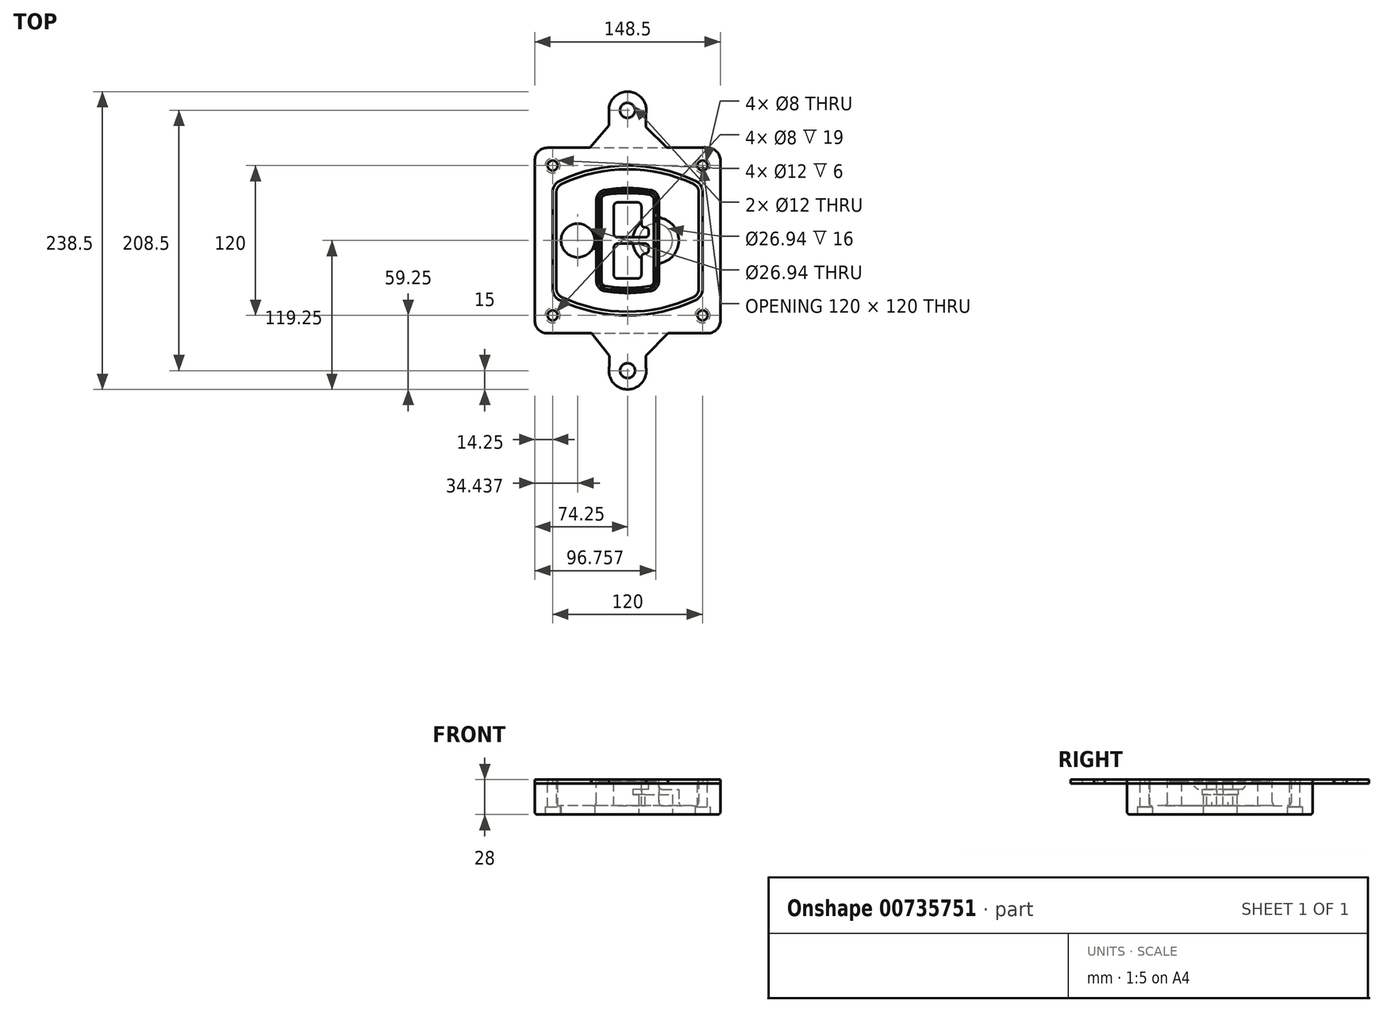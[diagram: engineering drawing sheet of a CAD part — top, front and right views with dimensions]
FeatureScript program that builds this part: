
annotation { "Feature Type Name" : "Feature", "Feature Type Description" : "" }
export const myFeature = defineFeature(function(context is Context, id is Id, definition is map)
    precondition{}
    {
        {
            var Q0;
            Q0=qCreatedBy(makeId("Top.planeOp"),FACE);
            var sketch = newSketch(context, id + "F0", { "sketchPlane" : qUnion([Q0])});
            skPoint(sketch, "E0.rect.middle", {"position": v(0, 0) * mm});
            skLineSegment(sketch, "E1.bottom", {"start": v(-64.25, -74.25) * mm, "end": v(64.25, -74.25) * mm});
            skLineSegment(sketch, "E1.top", {"start": v(-64.25, 74.25) * mm, "end": v(64.25, 74.25) * mm});
            skLineSegment(sketch, "E1.left", {"start": v(-74.25, -64.25) * mm, "end": v(-74.25, 64.25) * mm});
            skLineSegment(sketch, "E1.right", {"start": v(74.25, -64.25) * mm, "end": v(74.25, 64.25) * mm});
            skLineSegment(sketch, "E2", {"start": v(-74.25, 74.25) * mm, "end": v(74.25, -74.25) * mm, "construction": true});
            skLineSegment(sketch, "E3", {"start": v(74.25, 74.25) * mm, "end": v(-74.25, -74.25) * mm, "construction": true});
            skCircle(sketch, "E4", {"center": v(-60, 60) * mm, "radius": 4 * mm});
            skCircle(sketch, "E5", {"center": v(60, 60) * mm, "radius": 4 * mm});
            skCircle(sketch, "E6", {"center": v(60, -60) * mm, "radius": 4 * mm});
            skCircle(sketch, "E7", {"center": v(-60, -60) * mm, "radius": 4 * mm});
            skLineSegment(sketch, "E8", {"start": v(-60, 60) * mm, "end": v(60, 60) * mm, "construction": true});
            skLineSegment(sketch, "E9", {"start": v(60, 60) * mm, "end": v(60, -60) * mm, "construction": true});
            skLineSegment(sketch, "E10", {"start": v(60, -60) * mm, "end": v(-60, -60) * mm, "construction": true});
            skLineSegment(sketch, "E11", {"start": v(-60, -60) * mm, "end": v(-60, 60) * mm, "construction": true});
            skLineSegment(sketch, "E12", {"start": v(-60, 38.83) * mm, "end": v(-60, -38.83) * mm});
            skLineSegment(sketch, "E13", {"start": v(60, 38.83) * mm, "end": v(60, -38.83) * mm});
            skArc(sketch, "E14", {"start": v(54.26, 47.88) * mm, "mid": v(0, 60) * mm, "end": v(-54.26, 47.88) * mm});
            skArc(sketch, "E15", {"start": v(-54.26, -47.88) * mm, "mid": v(0, -60) * mm, "end": v(54.26, -47.88) * mm});
            skLineSegment(sketch, "E16", {"start": v(-60, 0) * mm, "end": v(60, 0) * mm, "construction": true});
            skPoint(sketch, "E17.visualSharp", {"position": v(-60, -45) * mm});
            skArc(sketch, "E17.filletArc", {"start": v(-60, -38.83) * mm, "mid": v(-58.44, -44.2) * mm, "end": v(-54.26, -47.88) * mm});
            skPoint(sketch, "E18.visualSharp", {"position": v(-60, 45) * mm});
            skArc(sketch, "E18.filletArc", {"start": v(-54.26, 47.88) * mm, "mid": v(-58.44, 44.2) * mm, "end": v(-60, 38.83) * mm});
            skPoint(sketch, "E19.visualSharp", {"position": v(60, 45) * mm});
            skArc(sketch, "E19.filletArc", {"start": v(60, 38.83) * mm, "mid": v(58.44, 44.2) * mm, "end": v(54.26, 47.88) * mm});
            skPoint(sketch, "E20.visualSharp", {"position": v(60, -45) * mm});
            skArc(sketch, "E20.filletArc", {"start": v(54.26, -47.88) * mm, "mid": v(58.44, -44.2) * mm, "end": v(60, -38.83) * mm});
            skPoint(sketch, "E21.visualSharp", {"position": v(-74.25, 74.25) * mm});
            skArc(sketch, "E21.filletArc", {"start": v(-64.25, 74.25) * mm, "mid": v(-71.32, 71.32) * mm, "end": v(-74.25, 64.25) * mm});
            skPoint(sketch, "E22.visualSharp", {"position": v(74.25, 74.25) * mm});
            skArc(sketch, "E22.filletArc", {"start": v(74.25, 64.25) * mm, "mid": v(71.32, 71.32) * mm, "end": v(64.25, 74.25) * mm});
            skPoint(sketch, "E23.visualSharp", {"position": v(74.25, -74.25) * mm});
            skArc(sketch, "E23.filletArc", {"start": v(64.25, -74.25) * mm, "mid": v(71.32, -71.32) * mm, "end": v(74.25, -64.25) * mm});
            skPoint(sketch, "E24.visualSharp", {"position": v(-74.25, -74.25) * mm});
            skArc(sketch, "E24.filletArc", {"start": v(-74.25, -64.25) * mm, "mid": v(-71.32, -71.32) * mm, "end": v(-64.25, -74.25) * mm});
            skArc(sketch, "E25.0", {"start": v(57, 38.83) * mm, "mid": v(55.9, 42.58) * mm, "end": v(52.98, 45.17) * mm});
            skLineSegment(sketch, "E25.1", {"start": v(57, 38.83) * mm, "end": v(57, -38.83) * mm});
            skArc(sketch, "E25.2", {"start": v(52.98, -45.17) * mm, "mid": v(55.9, -42.58) * mm, "end": v(57, -38.83) * mm});
            skArc(sketch, "E25.3", {"start": v(-52.98, -45.17) * mm, "mid": v(0, -57) * mm, "end": v(52.98, -45.17) * mm});
            skArc(sketch, "E25.4", {"start": v(-57, -38.83) * mm, "mid": v(-55.9, -42.58) * mm, "end": v(-52.98, -45.17) * mm});
            skArc(sketch, "E25.5", {"start": v(52.98, 45.17) * mm, "mid": v(0, 57) * mm, "end": v(-52.98, 45.17) * mm});
            skLineSegment(sketch, "E25.6", {"start": v(-57, 38.83) * mm, "end": v(-57, -38.83) * mm});
            skArc(sketch, "E25.7", {"start": v(-52.98, 45.17) * mm, "mid": v(-55.9, 42.58) * mm, "end": v(-57, 38.83) * mm});
            skArc(sketch, "E26.0", {"start": v(-55.96, 51.5) * mm, "mid": v(-61.82, 46.33) * mm, "end": v(-64, 38.83) * mm});
            skArc(sketch, "E26.1", {"start": v(55.96, 51.5) * mm, "mid": v(0, 64) * mm, "end": v(-55.96, 51.5) * mm});
            skArc(sketch, "E26.2", {"start": v(64, 38.83) * mm, "mid": v(61.82, 46.33) * mm, "end": v(55.96, 51.5) * mm});
            skLineSegment(sketch, "E26.3", {"start": v(64, 38.83) * mm, "end": v(64, -38.83) * mm});
            skArc(sketch, "E26.4", {"start": v(55.96, -51.5) * mm, "mid": v(61.82, -46.33) * mm, "end": v(64, -38.83) * mm});
            skLineSegment(sketch, "E26.5", {"start": v(-64, 38.83) * mm, "end": v(-64, -38.83) * mm});
            skArc(sketch, "E26.6", {"start": v(-55.96, -51.5) * mm, "mid": v(0, -64) * mm, "end": v(55.96, -51.5) * mm});
            skArc(sketch, "E26.7", {"start": v(-64, -38.83) * mm, "mid": v(-61.82, -46.33) * mm, "end": v(-55.96, -51.5) * mm});
            skSolve(sketch);
        }
        {
            var Q0;
            Q0=makeQuery(id+"F0.imprint","IMPRINT",FACE,{"disambiguationData":[TD([[makeQuery(id+"F0.imprint","IMPRINT",EDGE,{"derivedFrom":sQuery(id+"F0.wireOp",EDGE,"E1.bottom")}),1.0]])]});
            var Q1;
            Q1=makeQuery(id+"F0.imprint","IMPRINT",FACE,{"disambiguationData":[TD([[makeQuery(id+"F0.imprint","IMPRINT",EDGE,{"derivedFrom":sQuery(id+"F0.wireOp",EDGE,"E12")}),1.0]])]});
            var Q2;
            Q2=makeQuery(id+"F0.imprint","IMPRINT",FACE,{"disambiguationData":[TD([[makeQuery(id+"F0.imprint","IMPRINT",EDGE,{"derivedFrom":sQuery(id+"F0.wireOp",EDGE,"E25.0")}),1.0]])]});
            var Q3;
            Q3=makeQuery(id+"F0.imprint","IMPRINT",FACE,{"disambiguationData":[TD([[makeQuery(id+"F0.imprint","IMPRINT",EDGE,{"derivedFrom":sQuery(id+"F0.wireOp",EDGE,"E12")}),-1.0]])]});
            extrude(context, id + "F1", {"entities" : qUnion([Q0, Q1, Q2, Q3]), "oppositeDirection" : true, "depth" : 25 * mm});
        }
        {
            var Q0;
            Q0=makeQuery(id+"F0.imprint","IMPRINT",FACE,{"disambiguationData":[TD([[makeQuery(id+"F0.imprint","IMPRINT",EDGE,{"derivedFrom":sQuery(id+"F0.wireOp",EDGE,"E12")}),1.0]])]});
            extrude(context, id + "F2", {"entities" : qUnion([Q0]), "operationType" : NewBodyOperationType.ADD, "depth" : 3 * mm});
        }
        {
            var Q0;
            Q0=makeQuery(id+"F0.imprint","IMPRINT",FACE,{"disambiguationData":[TD([[makeQuery(id+"F0.imprint","IMPRINT",EDGE,{"derivedFrom":sQuery(id+"F0.wireOp",EDGE,"E25.0")}),1.0]])]});
            extrude(context, id + "F3", {"entities" : qUnion([Q0]), "operationType" : NewBodyOperationType.REMOVE, "oppositeDirection" : true, "depth" : 18 * mm});
        }
        {
            var Q0;
            Q0=makeQuery(id+"F2.opExtrude","CAP_FACE",FACE,{"disambiguationData":[OSD([sQuery(id+"F0.wireOp",EDGE,"E12"),sQuery(id+"F0.wireOp",EDGE,"E13"),sQuery(id+"F0.wireOp",EDGE,"E14"),sQuery(id+"F0.wireOp",EDGE,"E15"),sQuery(id+"F0.wireOp",EDGE,"E17.filletArc"),sQuery(id+"F0.wireOp",EDGE,"E18.filletArc"),sQuery(id+"F0.wireOp",EDGE,"E19.filletArc"),sQuery(id+"F0.wireOp",EDGE,"E20.filletArc"),sQuery(id+"F0.wireOp",EDGE,"E25.0"),sQuery(id+"F0.wireOp",EDGE,"E25.1"),sQuery(id+"F0.wireOp",EDGE,"E25.2"),sQuery(id+"F0.wireOp",EDGE,"E25.3"),sQuery(id+"F0.wireOp",EDGE,"E25.4"),sQuery(id+"F0.wireOp",EDGE,"E25.5"),sQuery(id+"F0.wireOp",EDGE,"E25.6"),sQuery(id+"F0.wireOp",EDGE,"E25.7")])],"isStart":false});
            var sketch = newSketch(context, id + "F4", { "sketchPlane" : qUnion([Q0])});
            skArc(sketch, "E27.0", {"start": v(-18.34, -40.45) * mm, "mid": v(0, -42) * mm, "end": v(18.34, -40.45) * mm});
            skArc(sketch, "E28.0", {"start": v(18.34, 40.45) * mm, "mid": v(0, 42) * mm, "end": v(-18.34, 40.45) * mm});
            skLineSegment(sketch, "E29", {"start": v(-25, 32.57) * mm, "end": v(-25, -32.57) * mm});
            skLineSegment(sketch, "E30", {"start": v(25, 32.57) * mm, "end": v(25, -32.57) * mm});
            skLineSegment(sketch, "E31", {"start": v(-25, 39.1) * mm, "end": v(25, 39.1) * mm, "construction": true});
            skLineSegment(sketch, "E32", {"start": v(-25, -39.1) * mm, "end": v(25, -39.1) * mm, "construction": true});
            skPoint(sketch, "E33.visualSharp", {"position": v(-25, 39.1) * mm});
            skArc(sketch, "E33.filletArc", {"start": v(-18.34, 40.45) * mm, "mid": v(-23.11, 37.73) * mm, "end": v(-25, 32.57) * mm});
            skPoint(sketch, "E34.visualSharp", {"position": v(25, 39.1) * mm});
            skArc(sketch, "E34.filletArc", {"start": v(25, 32.57) * mm, "mid": v(23.11, 37.73) * mm, "end": v(18.34, 40.45) * mm});
            skPoint(sketch, "E35.visualSharp", {"position": v(25, -39.1) * mm});
            skArc(sketch, "E35.filletArc", {"start": v(18.34, -40.45) * mm, "mid": v(23.11, -37.73) * mm, "end": v(25, -32.57) * mm});
            skPoint(sketch, "E36.visualSharp", {"position": v(-25, -39.1) * mm});
            skArc(sketch, "E36.filletArc", {"start": v(-25, -32.57) * mm, "mid": v(-23.11, -37.73) * mm, "end": v(-18.34, -40.45) * mm});
            skArc(sketch, "E37.0", {"start": v(52.98, 45.17) * mm, "mid": v(0, 57) * mm, "end": v(-52.98, 45.17) * mm});
            skArc(sketch, "E37.1", {"start": v(-52.98, 45.17) * mm, "mid": v(-55.9, 42.58) * mm, "end": v(-57, 38.83) * mm});
            skLineSegment(sketch, "E37.2", {"start": v(-57, 38.83) * mm, "end": v(-57, -38.83) * mm});
            skArc(sketch, "E37.3", {"start": v(-57, -38.83) * mm, "mid": v(-55.9, -42.58) * mm, "end": v(-52.98, -45.17) * mm});
            skArc(sketch, "E37.4", {"start": v(-52.98, -45.17) * mm, "mid": v(0, -57) * mm, "end": v(52.98, -45.17) * mm});
            skArc(sketch, "E37.5", {"start": v(52.98, -45.17) * mm, "mid": v(55.9, -42.58) * mm, "end": v(57, -38.83) * mm});
            skLineSegment(sketch, "E37.6", {"start": v(57, 38.83) * mm, "end": v(57, -38.83) * mm});
            skArc(sketch, "E37.7", {"start": v(57, 38.83) * mm, "mid": v(55.9, 42.58) * mm, "end": v(52.98, 45.17) * mm});
            skLineSegment(sketch, "E38.0", {"start": v(23, 32.57) * mm, "end": v(23, -32.57) * mm});
            skArc(sketch, "E38.1", {"start": v(18, -38.48) * mm, "mid": v(21.58, -36.44) * mm, "end": v(23, -32.57) * mm});
            skArc(sketch, "E38.2", {"start": v(-18, -38.48) * mm, "mid": v(0, -40) * mm, "end": v(18, -38.48) * mm});
            skArc(sketch, "E38.3", {"start": v(-23, -32.57) * mm, "mid": v(-21.58, -36.44) * mm, "end": v(-18, -38.48) * mm});
            skLineSegment(sketch, "E38.4", {"start": v(-23, 32.57) * mm, "end": v(-23, -32.57) * mm});
            skArc(sketch, "E38.5", {"start": v(23, 32.57) * mm, "mid": v(21.58, 36.44) * mm, "end": v(18, 38.48) * mm});
            skArc(sketch, "E38.6", {"start": v(-18, 38.48) * mm, "mid": v(-21.58, 36.44) * mm, "end": v(-23, 32.57) * mm});
            skArc(sketch, "E38.7", {"start": v(18, 38.48) * mm, "mid": v(0, 40) * mm, "end": v(-18, 38.48) * mm});
            skArc(sketch, "E39.0", {"start": v(21, 32.57) * mm, "mid": v(20.06, 35.15) * mm, "end": v(17.67, 36.5) * mm});
            skLineSegment(sketch, "E39.1", {"start": v(21, 32.57) * mm, "end": v(21, -32.57) * mm});
            skArc(sketch, "E39.2", {"start": v(17.67, -36.5) * mm, "mid": v(20.06, -35.15) * mm, "end": v(21, -32.57) * mm});
            skArc(sketch, "E39.3", {"start": v(-17.67, -36.5) * mm, "mid": v(0, -38) * mm, "end": v(17.67, -36.5) * mm});
            skArc(sketch, "E39.4", {"start": v(-21, -32.57) * mm, "mid": v(-20.06, -35.15) * mm, "end": v(-17.67, -36.5) * mm});
            skArc(sketch, "E39.5", {"start": v(17.67, 36.5) * mm, "mid": v(0, 38) * mm, "end": v(-17.67, 36.5) * mm});
            skLineSegment(sketch, "E39.6", {"start": v(-21, 32.57) * mm, "end": v(-21, -32.57) * mm});
            skArc(sketch, "E39.7", {"start": v(-17.67, 36.5) * mm, "mid": v(-20.06, 35.15) * mm, "end": v(-21, 32.57) * mm});
            skLineSegment(sketch, "E40", {"start": v(-25, 0) * mm, "end": v(25, 0) * mm, "construction": true});
            skLineSegment(sketch, "E41", {"start": v(-11, 5.5) * mm, "end": v(-11, 27.5) * mm});
            skLineSegment(sketch, "E42", {"start": v(-8, 30.5) * mm, "end": v(8, 30.5) * mm});
            skLineSegment(sketch, "E43", {"start": v(11, 27.5) * mm, "end": v(11, 13.5) * mm});
            skLineSegment(sketch, "E44", {"start": v(14, 10.5) * mm, "end": v(14, 10.5) * mm});
            skLineSegment(sketch, "E45", {"start": v(17, 7.5) * mm, "end": v(17, 5.5) * mm});
            skLineSegment(sketch, "E46", {"start": v(14, 2.5) * mm, "end": v(-8, 2.5) * mm});
            skPoint(sketch, "E47.visualSharp", {"position": v(-11, 30.5) * mm});
            skArc(sketch, "E47.filletArc", {"start": v(-8, 30.5) * mm, "mid": v(-10.12, 29.62) * mm, "end": v(-11, 27.5) * mm});
            skPoint(sketch, "E48.visualSharp", {"position": v(11, 30.5) * mm});
            skArc(sketch, "E48.filletArc", {"start": v(11, 27.5) * mm, "mid": v(10.12, 29.62) * mm, "end": v(8, 30.5) * mm});
            skPoint(sketch, "E49.visualSharp", {"position": v(11, 10.5) * mm});
            skArc(sketch, "E49.filletArc", {"start": v(11, 13.5) * mm, "mid": v(11.88, 11.38) * mm, "end": v(14, 10.5) * mm});
            skPoint(sketch, "E50.visualSharp", {"position": v(17, 10.5) * mm});
            skArc(sketch, "E50.filletArc", {"start": v(17, 7.5) * mm, "mid": v(16.12, 9.62) * mm, "end": v(14, 10.5) * mm});
            skPoint(sketch, "E51.visualSharp", {"position": v(17, 2.5) * mm});
            skArc(sketch, "E51.filletArc", {"start": v(14, 2.5) * mm, "mid": v(16.12, 3.38) * mm, "end": v(17, 5.5) * mm});
            skPoint(sketch, "E52.visualSharp", {"position": v(-11, 2.5) * mm});
            skArc(sketch, "E52.filletArc", {"start": v(-11, 5.5) * mm, "mid": v(-10.12, 3.38) * mm, "end": v(-8, 2.5) * mm});
            skLineSegment(sketch, "E53.0.MirrorCS", {"start": v(14, -2.5) * mm, "end": v(-8, -2.5) * mm});
            skArc(sketch, "E54.0.MirrorCS", {"start": v(-11, -5.5) * mm, "mid": v(-10.12, -3.38) * mm, "end": v(-8, -2.5) * mm});
            skLineSegment(sketch, "E55.0.MirrorCS", {"start": v(-11, -5.5) * mm, "end": v(-11, -27.5) * mm});
            skArc(sketch, "E56.0.MirrorCS", {"start": v(-8, -30.5) * mm, "mid": v(-10.12, -29.62) * mm, "end": v(-11, -27.5) * mm});
            skLineSegment(sketch, "E57.0.MirrorCS", {"start": v(-8, -30.5) * mm, "end": v(8, -30.5) * mm});
            skArc(sketch, "E58.0.MirrorCS", {"start": v(11, -27.5) * mm, "mid": v(10.12, -29.62) * mm, "end": v(8, -30.5) * mm});
            skLineSegment(sketch, "E59.0.MirrorCS", {"start": v(11, -27.5) * mm, "end": v(11, -13.5) * mm});
            skArc(sketch, "E60.0.MirrorCS", {"start": v(11, -13.5) * mm, "mid": v(11.88, -11.38) * mm, "end": v(14, -10.5) * mm});
            skArc(sketch, "E61.0.MirrorCS", {"start": v(17, -7.5) * mm, "mid": v(16.12, -9.62) * mm, "end": v(14, -10.5) * mm});
            skLineSegment(sketch, "E62.0.MirrorCS", {"start": v(17, -7.5) * mm, "end": v(17, -5.5) * mm});
            skArc(sketch, "E63.0.MirrorCS", {"start": v(14, -2.5) * mm, "mid": v(16.12, -3.38) * mm, "end": v(17, -5.5) * mm});
            skSolve(sketch);
        }
        {
            var Q0;
            Q0=makeQuery(id+"F4.imprint","IMPRINT",FACE,{"disambiguationData":[TD([[makeQuery(id+"F4.imprint","IMPRINT",EDGE,{"derivedFrom":sQuery(id+"F4.wireOp",EDGE,"E27.0")}),1.0]])]});
            var Q1;
            Q1=makeQuery(id+"F4.imprint","IMPRINT",FACE,{"disambiguationData":[TD([[makeQuery(id+"F4.imprint","IMPRINT",EDGE,{"derivedFrom":sQuery(id+"F4.wireOp",EDGE,"E38.0")}),-1.0]])]});
            var Q2;
            Q2=makeQuery(id+"F4.imprint","IMPRINT",FACE,{"disambiguationData":[TD([[makeQuery(id+"F4.imprint","IMPRINT",EDGE,{"derivedFrom":sQuery(id+"F4.wireOp",EDGE,"E39.0")}),1.0]])]});
            extrude(context, id + "F5", {"entities" : qUnion([Q0, Q1, Q2]), "operationType" : NewBodyOperationType.ADD, "endBound" : BoundingType.UP_TO_NEXT, "oppositeDirection" : true, "depth" : 25 * mm});
        }
        {
            var Q0;
            Q0=makeQuery(id+"F4.imprint","IMPRINT",FACE,{"disambiguationData":[TD([[makeQuery(id+"F4.imprint","IMPRINT",EDGE,{"derivedFrom":sQuery(id+"F4.wireOp",EDGE,"E38.0")}),-1.0]])]});
            extrude(context, id + "F6", {"entities" : qUnion([Q0]), "operationType" : NewBodyOperationType.REMOVE, "oppositeDirection" : true, "depth" : 2 * mm});
        }
        {
            var Q0;
            Q0=makeQuery(id+"F1.opExtrude","CAP_FACE",FACE,{"disambiguationData":[OSD([sQuery(id+"F0.wireOp",EDGE,"E1.bottom"),sQuery(id+"F0.wireOp",EDGE,"E1.top"),sQuery(id+"F0.wireOp",EDGE,"E1.left"),sQuery(id+"F0.wireOp",EDGE,"E1.right"),sQuery(id+"F0.wireOp",EDGE,"E4"),sQuery(id+"F0.wireOp",EDGE,"E5"),sQuery(id+"F0.wireOp",EDGE,"E6"),sQuery(id+"F0.wireOp",EDGE,"E7"),sQuery(id+"F0.wireOp",EDGE,"E21.filletArc"),sQuery(id+"F0.wireOp",EDGE,"E22.filletArc"),sQuery(id+"F0.wireOp",EDGE,"E23.filletArc"),sQuery(id+"F0.wireOp",EDGE,"E24.filletArc")])],"isStart":false});
            var sketch = newSketch(context, id + "F7", { "sketchPlane" : qUnion([Q0])});
            skCircle(sketch, "E64", {"center": v(22.5, 0) * mm, "radius": 13.47 * mm});
            skCircle(sketch, "E65", {"center": v(-39.81, 0) * mm, "radius": 13.47 * mm});
            skLineSegment(sketch, "E66", {"start": v(74.25, 0) * mm, "end": v(-74.25, 0) * mm});
            skCircle(sketch, "E67", {"center": v(22.5, 0) * mm, "radius": 18.47 * mm});
            skCircle(sketch, "E68", {"center": v(60, -60) * mm, "radius": 6 * mm});
            skCircle(sketch, "E69", {"center": v(-60, -60) * mm, "radius": 6 * mm});
            skCircle(sketch, "E70", {"center": v(-60, 60) * mm, "radius": 6 * mm});
            skCircle(sketch, "E71", {"center": v(60, 60) * mm, "radius": 6 * mm});
            skSolve(sketch);
        }
        {
            var Q0;
            {var subQ1=sQuery(id+"F7.wireOp",EDGE,"E66");var subQ4=sQuery(id+"F7.wireOp",EDGE,"E64");var subQ6=makeQuery(id+"F7.imprint","INTERSECT",VERTEX,{"disambiguationData":[OD(0.0)],"derivedFrom":[subQ4,subQ1]});Q0=makeQuery(id+"F7.imprint","IMPRINT",FACE,{"disambiguationData":[TD([[makeQuery(id+"F7.imprint","IMPRINT",EDGE,{"disambiguationData":[TD([[subQ6,-1.0]])],"derivedFrom":subQ4}),-1.0]])]});}
            var Q1;
            {var subQ0=sQuery(id+"F7.wireOp",EDGE,"E66");var subQ1=sQuery(id+"F7.wireOp",EDGE,"E64");var subQ3=makeQuery(id+"F7.imprint","INTERSECT",VERTEX,{"disambiguationData":[OD(0.0)],"derivedFrom":[subQ1,subQ0]});Q1=makeQuery(id+"F7.imprint","IMPRINT",FACE,{"disambiguationData":[TD([[makeQuery(id+"F7.imprint","IMPRINT",EDGE,{"disambiguationData":[TD([[subQ3,-1.0]])],"derivedFrom":subQ1}),1.0]])]});}
            var Q2;
            {var subQ0=sQuery(id+"F7.wireOp",EDGE,"E66");var subQ1=sQuery(id+"F7.wireOp",EDGE,"E64");var subQ3=makeQuery(id+"F7.imprint","INTERSECT",VERTEX,{"disambiguationData":[OD(0.0)],"derivedFrom":[subQ1,subQ0]});Q2=makeQuery(id+"F7.imprint","IMPRINT",FACE,{"disambiguationData":[TD([[makeQuery(id+"F7.imprint","IMPRINT",EDGE,{"disambiguationData":[TD([[subQ3,1.0]])],"derivedFrom":subQ1}),1.0]])]});}
            var Q3;
            {var subQ1=sQuery(id+"F7.wireOp",EDGE,"E66");var subQ4=sQuery(id+"F7.wireOp",EDGE,"E64");var subQ6=makeQuery(id+"F7.imprint","INTERSECT",VERTEX,{"disambiguationData":[OD(0.0)],"derivedFrom":[subQ4,subQ1]});Q3=makeQuery(id+"F7.imprint","IMPRINT",FACE,{"disambiguationData":[TD([[makeQuery(id+"F7.imprint","IMPRINT",EDGE,{"disambiguationData":[TD([[subQ6,1.0]])],"derivedFrom":subQ4}),-1.0]])]});}
            extrude(context, id + "F8", {"entities" : qUnion([Q0, Q1, Q2, Q3]), "operationType" : NewBodyOperationType.ADD, "oppositeDirection" : true, "depth" : 20 * mm});
        }
        {
            var Q0;
            {var subQ0=sQuery(id+"F7.wireOp",EDGE,"E66");var subQ1=sQuery(id+"F7.wireOp",EDGE,"E64");var subQ3=makeQuery(id+"F7.imprint","INTERSECT",VERTEX,{"disambiguationData":[OD(0.0)],"derivedFrom":[subQ1,subQ0]});Q0=makeQuery(id+"F7.imprint","IMPRINT",FACE,{"disambiguationData":[TD([[makeQuery(id+"F7.imprint","IMPRINT",EDGE,{"disambiguationData":[TD([[subQ3,-1.0]])],"derivedFrom":subQ1}),1.0]])]});}
            var Q1;
            {var subQ0=sQuery(id+"F7.wireOp",EDGE,"E66");var subQ1=sQuery(id+"F7.wireOp",EDGE,"E64");var subQ3=makeQuery(id+"F7.imprint","INTERSECT",VERTEX,{"disambiguationData":[OD(0.0)],"derivedFrom":[subQ1,subQ0]});Q1=makeQuery(id+"F7.imprint","IMPRINT",FACE,{"disambiguationData":[TD([[makeQuery(id+"F7.imprint","IMPRINT",EDGE,{"disambiguationData":[TD([[subQ3,1.0]])],"derivedFrom":subQ1}),1.0]])]});}
            extrude(context, id + "F9", {"entities" : qUnion([Q0, Q1]), "operationType" : NewBodyOperationType.REMOVE, "oppositeDirection" : true, "depth" : 16 * mm});
        }
        {
            var Q0;
            {var subQ0=sQuery(id+"F7.wireOp",EDGE,"E66");var subQ1=sQuery(id+"F7.wireOp",EDGE,"E65");var subQ3=makeQuery(id+"F7.imprint","INTERSECT",VERTEX,{"disambiguationData":[OD(0.0)],"derivedFrom":[subQ1,subQ0]});Q0=makeQuery(id+"F7.imprint","IMPRINT",FACE,{"disambiguationData":[TD([[makeQuery(id+"F7.imprint","IMPRINT",EDGE,{"disambiguationData":[TD([[subQ3,-1.0]])],"derivedFrom":subQ1}),1.0]])]});}
            var Q1;
            {var subQ0=sQuery(id+"F7.wireOp",EDGE,"E66");var subQ1=sQuery(id+"F7.wireOp",EDGE,"E65");var subQ3=makeQuery(id+"F7.imprint","INTERSECT",VERTEX,{"disambiguationData":[OD(0.0)],"derivedFrom":[subQ1,subQ0]});Q1=makeQuery(id+"F7.imprint","IMPRINT",FACE,{"disambiguationData":[TD([[makeQuery(id+"F7.imprint","IMPRINT",EDGE,{"disambiguationData":[TD([[subQ3,1.0]])],"derivedFrom":subQ1}),1.0]])]});}
            extrude(context, id + "F10", {"entities" : qUnion([Q0, Q1]), "operationType" : NewBodyOperationType.REMOVE, "oppositeDirection" : true, "depth" : 25 * mm});
        }
        {
            var Q0;
            Q0=makeQuery(id+"F7.imprint","IMPRINT",FACE,{"disambiguationData":[TD([[makeQuery(id+"F7.imprint","IMPRINT",EDGE,{"derivedFrom":sQuery(id+"F7.wireOp",EDGE,"E68")}),1.0]])]});
            var Q1;
            Q1=makeQuery(id+"F7.imprint","IMPRINT",FACE,{"disambiguationData":[TD([[makeQuery(id+"F7.imprint","IMPRINT",EDGE,{"derivedFrom":makeQuery(id+"F1.opExtrude","CAP_EDGE",EDGE,{"disambiguationData":[OSD([sQuery(id+"F0.wireOp",EDGE,"E5")])],"isStart":false})}),-1.0]])]});
            var Q2;
            Q2=makeQuery(id+"F7.imprint","IMPRINT",FACE,{"disambiguationData":[TD([[makeQuery(id+"F7.imprint","IMPRINT",EDGE,{"derivedFrom":sQuery(id+"F7.wireOp",EDGE,"E69")}),1.0]])]});
            var Q3;
            Q3=makeQuery(id+"F7.imprint","IMPRINT",FACE,{"disambiguationData":[TD([[makeQuery(id+"F7.imprint","IMPRINT",EDGE,{"derivedFrom":makeQuery(id+"F1.opExtrude","CAP_EDGE",EDGE,{"disambiguationData":[OSD([sQuery(id+"F0.wireOp",EDGE,"E4")])],"isStart":false})}),-1.0]])]});
            var Q4;
            Q4=makeQuery(id+"F7.imprint","IMPRINT",FACE,{"disambiguationData":[TD([[makeQuery(id+"F7.imprint","IMPRINT",EDGE,{"derivedFrom":sQuery(id+"F7.wireOp",EDGE,"E70")}),1.0]])]});
            var Q5;
            Q5=makeQuery(id+"F7.imprint","IMPRINT",FACE,{"disambiguationData":[TD([[makeQuery(id+"F7.imprint","IMPRINT",EDGE,{"derivedFrom":makeQuery(id+"F1.opExtrude","CAP_EDGE",EDGE,{"disambiguationData":[OSD([sQuery(id+"F0.wireOp",EDGE,"E7")])],"isStart":false})}),-1.0]])]});
            var Q6;
            Q6=makeQuery(id+"F7.imprint","IMPRINT",FACE,{"disambiguationData":[TD([[makeQuery(id+"F7.imprint","IMPRINT",EDGE,{"derivedFrom":sQuery(id+"F7.wireOp",EDGE,"E71")}),1.0]])]});
            var Q7;
            Q7=makeQuery(id+"F7.imprint","IMPRINT",FACE,{"disambiguationData":[TD([[makeQuery(id+"F7.imprint","IMPRINT",EDGE,{"derivedFrom":makeQuery(id+"F1.opExtrude","CAP_EDGE",EDGE,{"disambiguationData":[OSD([sQuery(id+"F0.wireOp",EDGE,"E6")])],"isStart":false})}),-1.0]])]});
            extrude(context, id + "F11", {"entities" : qUnion([Q0, Q1, Q2, Q3, Q4, Q5, Q6, Q7]), "operationType" : NewBodyOperationType.REMOVE, "oppositeDirection" : true, "depth" : 6 * mm});
        }
        {
            var Q0;
            Q0=makeQuery(id+"F9.boolean.opBoolean","COPY",FACE,{"derivedFrom":makeQuery(id+"F9.opExtrude","CAP_FACE",FACE,{"disambiguationData":[OSD([sQuery(id+"F7.wireOp",EDGE,"E64")])],"isStart":false})});
            var sketch = newSketch(context, id + "F12", { "sketchPlane" : qUnion([Q0])});
            skArc(sketch, "E72.0", {"start": v(11, 14.45) * mm, "mid": v(6.45, 9.13) * mm, "end": v(4.2, 2.5) * mm});
            skArc(sketch, "E72.1", {"start": v(4.2, -2.5) * mm, "mid": v(6.45, -9.13) * mm, "end": v(11, -14.45) * mm});
            skLineSegment(sketch, "E73", {"start": v(4.2, -2.5) * mm, "end": v(14, -2.5) * mm});
            skLineSegment(sketch, "E74.0", {"start": v(14, 2.5) * mm, "end": v(4.2, 2.5) * mm});
            skArc(sketch, "E74.1", {"start": v(14, 2.5) * mm, "mid": v(16.12, 3.38) * mm, "end": v(17, 5.5) * mm});
            skLineSegment(sketch, "E74.2", {"start": v(17, 7.5) * mm, "end": v(17, 5.5) * mm});
            skArc(sketch, "E74.3", {"start": v(17, 7.5) * mm, "mid": v(16.12, 9.62) * mm, "end": v(14, 10.5) * mm});
            skArc(sketch, "E74.4", {"start": v(11, 13.5) * mm, "mid": v(11.88, 11.38) * mm, "end": v(14, 10.5) * mm});
            skLineSegment(sketch, "E74.5", {"start": v(11, 14.45) * mm, "end": v(11, 13.5) * mm});
            skLineSegment(sketch, "E74.7", {"start": v(14, -2.5) * mm, "end": v(4.2, -2.5) * mm});
            skArc(sketch, "E74.8", {"start": v(14, -2.5) * mm, "mid": v(16.12, -3.38) * mm, "end": v(17, -5.5) * mm});
            skLineSegment(sketch, "E74.9", {"start": v(17, -7.5) * mm, "end": v(17, -5.5) * mm});
            skArc(sketch, "E74.10", {"start": v(17, -7.5) * mm, "mid": v(16.12, -9.62) * mm, "end": v(14, -10.5) * mm});
            skArc(sketch, "E74.11", {"start": v(11, -13.5) * mm, "mid": v(11.88, -11.38) * mm, "end": v(14, -10.5) * mm});
            skLineSegment(sketch, "E74.12", {"start": v(11, -14.45) * mm, "end": v(11, -13.5) * mm});
            skPoint(sketch, "E75.orphan", {"position": v(11, -27.5) * mm});
            skPoint(sketch, "E76.orphan", {"position": v(-8, -2.5) * mm});
            skPoint(sketch, "E77.orphan", {"position": v(-8, 2.5) * mm});
            skPoint(sketch, "E78.orphan", {"position": v(11, 27.5) * mm});
            skSolve(sketch);
        }
        {
            var Q0;
            {var subQ7=sQuery(id+"F12.wireOp",EDGE,"E72.0");var subQ14=sQuery(id+"F12.wireOp",EDGE,"E72.1");var subQ16=sQuery(id+"F12.wireOp",EDGE,"E74.1");var subQ18=sQuery(id+"F12.wireOp",EDGE,"E74.8");Q0=qUnion([makeQuery(id+"F12.imprint","IMPRINT",FACE,{"disambiguationData":[TD([[makeQuery(id+"F12.imprint","IMPRINT",EDGE,{"derivedFrom":subQ7}),1.0]])]}),makeQuery(id+"F12.imprint","IMPRINT",FACE,{"disambiguationData":[TD([[makeQuery(id+"F12.imprint","IMPRINT",EDGE,{"derivedFrom":subQ14}),1.0]])]}),makeQuery(id+"F12.imprint","IMPRINT",FACE,{"disambiguationData":[TD([[makeQuery(id+"F12.imprint","IMPRINT",EDGE,{"derivedFrom":subQ16}),1.0]])]}),makeQuery(id+"F12.imprint","IMPRINT",FACE,{"disambiguationData":[TD([[makeQuery(id+"F12.imprint","IMPRINT",EDGE,{"derivedFrom":subQ18}),-1.0]])]})]);}
            var Q1;
            Q1=makeQuery(id+"F5.boolean.opBoolean","SPLIT",FACE,{"disambiguationData":[TD([makeQuery(id+"F5.opExtrude","SWEPT_FACE",FACE,{"disambiguationData":[OSD([sQuery(id+"F4.wireOp",EDGE,"E41")])]})])],"derivedFrom":makeQuery(id+"F3.boolean.opBoolean","COPY",FACE,{"derivedFrom":makeQuery(id+"F3.opExtrude","CAP_FACE",FACE,{"disambiguationData":[OSD([sQuery(id+"F0.wireOp",EDGE,"E25.0"),sQuery(id+"F0.wireOp",EDGE,"E25.1"),sQuery(id+"F0.wireOp",EDGE,"E25.2"),sQuery(id+"F0.wireOp",EDGE,"E25.3"),sQuery(id+"F0.wireOp",EDGE,"E25.4"),sQuery(id+"F0.wireOp",EDGE,"E25.5"),sQuery(id+"F0.wireOp",EDGE,"E25.6"),sQuery(id+"F0.wireOp",EDGE,"E25.7")])],"isStart":false})})});
            extrude(context, id + "F13", {"entities" : qUnion([Q0]), "operationType" : NewBodyOperationType.REMOVE, "endBound" : BoundingType.UP_TO_SURFACE, "endBoundEntityFace" : qUnion([Q1]), "depth" : 25 * mm});
        }
        {
            var Q0;
            Q0=makeQuery(id+"F3.boolean.opBoolean","COPY",EDGE,{"derivedFrom":makeQuery(id+"F3.opExtrude","CAP_EDGE",EDGE,{"disambiguationData":[OSD([sQuery(id+"F0.wireOp",EDGE,"E25.6")])],"isStart":false})});
            var Q1;
            Q1=makeQuery(id+"F8.boolean.opBoolean","INTERSECT",EDGE,{"derivedFrom":[makeQuery(id+"F5.opExtrude","SWEPT_FACE",FACE,{"disambiguationData":[OSD([sQuery(id+"F4.wireOp",EDGE,"E30")])]}),makeQuery(id+"F8.opExtrude","CAP_FACE",FACE,{"disambiguationData":[OSD([sQuery(id+"F7.wireOp",EDGE,"E67")])],"isStart":false})]});
            var Q2;
            Q2=makeQuery(id+"F8.boolean.opBoolean","INTERSECT",EDGE,{"disambiguationData":[OD(1.0)],"derivedFrom":[makeQuery(id+"F5.opExtrude","SWEPT_FACE",FACE,{"disambiguationData":[OSD([sQuery(id+"F4.wireOp",EDGE,"E30")])]}),makeQuery(id+"F8.opExtrude","SWEPT_FACE",FACE,{"disambiguationData":[OSD([sQuery(id+"F7.wireOp",EDGE,"E67")])]})]});
            var Q3;
            {var subQ0=sQuery(id+"F4.wireOp",EDGE,"E30");Q3=makeQuery(id+"F8.boolean.opBoolean","SPLIT",EDGE,{"disambiguationData":[TD([makeQuery(id+"F5.opExtrude","SWEPT_FACE",FACE,{"disambiguationData":[OSD([sQuery(id+"F4.wireOp",EDGE,"E35.filletArc")])]})])],"derivedFrom":makeQuery(id+"F5.opExtrude","CAP_EDGE",EDGE,{"disambiguationData":[OSD([subQ0])],"isStart":false})});}
            var Q4;
            {var subQ0=sQuery(id+"F0.wireOp",EDGE,"E25.7");var subQ1=sQuery(id+"F0.wireOp",EDGE,"E25.1");var subQ2=sQuery(id+"F0.wireOp",EDGE,"E25.6");var subQ3=sQuery(id+"F0.wireOp",EDGE,"E25.5");var subQ4=sQuery(id+"F0.wireOp",EDGE,"E25.4");var subQ5=sQuery(id+"F0.wireOp",EDGE,"E25.0");var subQ6=sQuery(id+"F0.wireOp",EDGE,"E25.2");var subQ7=sQuery(id+"F0.wireOp",EDGE,"E25.3");Q4=makeQuery(id+"F8.boolean.opBoolean","INTERSECT",EDGE,{"derivedFrom":[makeQuery(id+"F5.boolean.opBoolean","SPLIT",FACE,{"disambiguationData":[TD([makeQuery(id+"F2.opExtrude","SWEPT_FACE",FACE,{"disambiguationData":[OSD([subQ5])]})])],"derivedFrom":makeQuery(id+"F3.boolean.opBoolean","COPY",FACE,{"derivedFrom":makeQuery(id+"F3.opExtrude","CAP_FACE",FACE,{"disambiguationData":[OSD([subQ5,subQ1,subQ6,subQ7,subQ4,subQ3,subQ2,subQ0])],"isStart":false})})}),makeQuery(id+"F8.opExtrude","SWEPT_FACE",FACE,{"disambiguationData":[OSD([sQuery(id+"F7.wireOp",EDGE,"E67")])]})]});}
            var Q5;
            Q5=makeQuery(id+"F8.boolean.opBoolean","INTERSECT",EDGE,{"disambiguationData":[OD(0.0)],"derivedFrom":[makeQuery(id+"F5.opExtrude","SWEPT_FACE",FACE,{"disambiguationData":[OSD([sQuery(id+"F4.wireOp",EDGE,"E30")])]}),makeQuery(id+"F8.opExtrude","SWEPT_FACE",FACE,{"disambiguationData":[OSD([sQuery(id+"F7.wireOp",EDGE,"E67")])]})]});
            fillet(context, id + "F14", {"entities" : qUnion([Q0, Q1, Q2, Q3, Q4, Q5]), "radius" : 3 * mm, "tangentPropagation" : true, "allowEdgeOverflow" : false});
        }
        {
            var Q0;
            Q0=makeQuery(id+"F1.opExtrude","CAP_EDGE",EDGE,{"disambiguationData":[OSD([sQuery(id+"F0.wireOp",EDGE,"E1.bottom")])],"isStart":false});
            fillet(context, id + "F15", {"entities" : qUnion([Q0]), "radius" : 2 * mm, "tangentPropagation" : true, "allowEdgeOverflow" : false});
        }
        {
            var Q0;
            {var subQ0=sQuery(id+"F0.wireOp",EDGE,"E21.filletArc");var subQ1=sQuery(id+"F0.wireOp",EDGE,"E7");var subQ2=sQuery(id+"F0.wireOp",EDGE,"E6");var subQ3=sQuery(id+"F0.wireOp",EDGE,"E5");var subQ4=sQuery(id+"F0.wireOp",EDGE,"E4");var subQ5=sQuery(id+"F0.wireOp",EDGE,"E22.filletArc");var subQ6=sQuery(id+"F0.wireOp",EDGE,"E1.bottom");var subQ7=sQuery(id+"F0.wireOp",EDGE,"E1.right");var subQ8=sQuery(id+"F0.wireOp",EDGE,"E1.top");var subQ9=sQuery(id+"F0.wireOp",EDGE,"E1.left");var subQ10=sQuery(id+"F0.wireOp",EDGE,"E23.filletArc");var subQ11=sQuery(id+"F0.wireOp",EDGE,"E24.filletArc");Q0=makeQuery(id+"F2.boolean.opBoolean","SPLIT",FACE,{"disambiguationData":[TD([makeQuery(id+"F1.opExtrude","SWEPT_FACE",FACE,{"disambiguationData":[OSD([subQ6])]})])],"derivedFrom":makeQuery(id+"F1.opExtrude","CAP_FACE",FACE,{"disambiguationData":[OSD([subQ6,subQ8,subQ9,subQ7,subQ4,subQ3,subQ2,subQ1,subQ0,subQ5,subQ10,subQ11])],"isStart":true})});}
            var sketch = newSketch(context, id + "F16", { "sketchPlane" : qUnion([Q0])});
            skPoint(sketch, "E79.start.orphan", {"position": v(0, 74.25) * mm});
            skLineSegment(sketch, "E80", {"start": v(0, 74.25) * mm, "end": v(0, 104.25) * mm, "construction": true});
            skCircle(sketch, "E81", {"center": v(0, 104.25) * mm, "radius": 6 * mm});
            skLineSegment(sketch, "E82", {"start": v(14.76, 90.95) * mm, "end": v(31.46, 74.25) * mm});
            skLineSegment(sketch, "E83", {"start": v(-14.76, 92.25) * mm, "end": v(-30.06, 74.25) * mm});
            skPoint(sketch, "E84.start.orphan", {"position": v(14.76, 101.6) * mm});
            skLineSegment(sketch, "E85", {"start": v(14.76, 101.6) * mm, "end": v(14.76, 90.95) * mm});
            skPoint(sketch, "E86.start.orphan", {"position": v(-14.76, 101.6) * mm});
            skLineSegment(sketch, "E87", {"start": v(-14.76, 101.6) * mm, "end": v(-14.76, 92.25) * mm});
            skArc(sketch, "E88", {"start": v(14.76, 101.6) * mm, "mid": v(0, 119.25) * mm, "end": v(-14.76, 101.6) * mm});
            skPoint(sketch, "E89.center.orphan", {"position": v(0.1, -65.21) * mm});
            skLineSegment(sketch, "E90", {"start": v(0, -74.25) * mm, "end": v(0, -104.25) * mm, "construction": true});
            skCircle(sketch, "E91", {"center": v(0, -104.25) * mm, "radius": 6 * mm});
            skLineSegment(sketch, "E92", {"start": v(32.63, -74.16) * mm, "end": v(14.54, -92.25) * mm});
            skLineSegment(sketch, "E93", {"start": v(14.54, -92.25) * mm, "end": v(14.54, -100.56) * mm});
            skLineSegment(sketch, "E94", {"start": v(-14.54, -92.25) * mm, "end": v(-14.54, -100.56) * mm});
            skArc(sketch, "E95", {"start": v(-14.54, -100.56) * mm, "mid": v(0, -119.25) * mm, "end": v(14.54, -100.56) * mm});
            skLineSegment(sketch, "E96", {"start": v(-14.54, -92.25) * mm, "end": v(-28.96, -74.25) * mm});
            skSolve(sketch);
        }
        {
            var Q0;
            Q0=makeQuery(id+"F16.imprint","IMPRINT",FACE,{"disambiguationData":[TD([[makeQuery(id+"F16.imprint","IMPRINT",EDGE,{"derivedFrom":makeQuery(id+"F1.opExtrude","CAP_EDGE",EDGE,{"disambiguationData":[OSD([sQuery(id+"F0.wireOp",EDGE,"E1.left")])],"isStart":true})}),-1.0]])]});
            var Q1;
            Q1=makeQuery(id+"F16.imprint","IMPRINT",FACE,{"disambiguationData":[TD([[makeQuery(id+"F16.imprint","IMPRINT",EDGE,{"derivedFrom":sQuery(id+"F16.wireOp",EDGE,"E91")}),-1.0]])]});
            var Q2;
            Q2=makeQuery(id+"F16.imprint","IMPRINT",FACE,{"disambiguationData":[TD([[makeQuery(id+"F16.imprint","IMPRINT",EDGE,{"derivedFrom":sQuery(id+"F16.wireOp",EDGE,"E81")}),-1.0]])]});
            var Q3;
            Q3=makeQuery(id+"F2.opExtrude","CAP_FACE",FACE,{"disambiguationData":[OSD([sQuery(id+"F0.wireOp",EDGE,"E12"),sQuery(id+"F0.wireOp",EDGE,"E13"),sQuery(id+"F0.wireOp",EDGE,"E14"),sQuery(id+"F0.wireOp",EDGE,"E15"),sQuery(id+"F0.wireOp",EDGE,"E17.filletArc"),sQuery(id+"F0.wireOp",EDGE,"E18.filletArc"),sQuery(id+"F0.wireOp",EDGE,"E19.filletArc"),sQuery(id+"F0.wireOp",EDGE,"E20.filletArc"),sQuery(id+"F0.wireOp",EDGE,"E25.0"),sQuery(id+"F0.wireOp",EDGE,"E25.1"),sQuery(id+"F0.wireOp",EDGE,"E25.2"),sQuery(id+"F0.wireOp",EDGE,"E25.3"),sQuery(id+"F0.wireOp",EDGE,"E25.4"),sQuery(id+"F0.wireOp",EDGE,"E25.5"),sQuery(id+"F0.wireOp",EDGE,"E25.6"),sQuery(id+"F0.wireOp",EDGE,"E25.7")])],"isStart":false});
            extrude(context, id + "F17", {"entities" : qUnion([Q0, Q1, Q2]), "endBound" : BoundingType.UP_TO_SURFACE, "depth" : 25 * mm, "endBoundEntityFace" : qUnion([Q3]), "offsetDistance" : 25 * mm});
        }
    });
